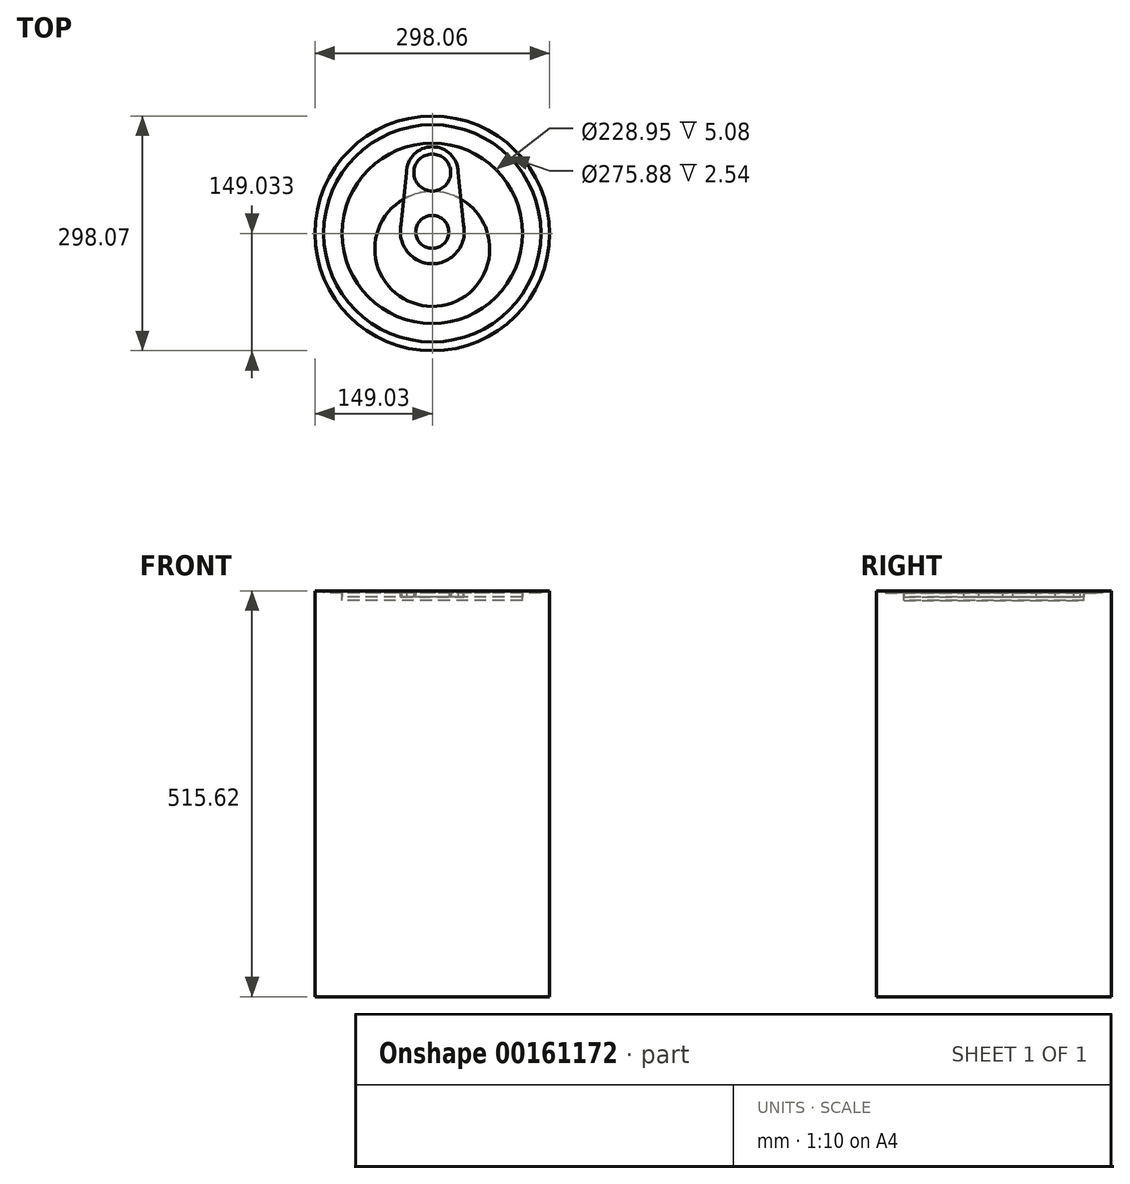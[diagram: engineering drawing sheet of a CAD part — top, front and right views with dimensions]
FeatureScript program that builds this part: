
annotation { "Feature Type Name" : "Feature", "Feature Type Description" : "" }
export const myFeature = defineFeature(function(context is Context, id is Id, definition is map)
    precondition{}
    {
        {
            var Q0;
            Q0=qCreatedBy(makeId("Top.planeOp"),FACE);
            var sketch = newSketch(context, id + "F0", { "sketchPlane" : qUnion([Q0])});
            skCircle(sketch, "E0", {"center": v(0, 0) * mm, "radius": 23.84 * mm});
            skCircle(sketch, "E1", {"center": v(0, 0) * mm, "radius": 32.37 * mm});
            skCircle(sketch, "E2", {"center": v(0, -75.39) * mm, "radius": 21.38 * mm});
            skCircle(sketch, "E3", {"center": v(0, -75.39) * mm, "radius": 40.12 * mm});
            skLineSegment(sketch, "E4", {"start": v(40.12, -76.22) * mm, "end": v(32.53, 0) * mm});
            skLineSegment(sketch, "E5", {"start": v(-32.37, 0) * mm, "end": v(-40.12, -76.25) * mm});
            skLineSegment(sketch, "E6", {"start": v(40.12, -76.22) * mm, "end": v(-40.12, -76.25) * mm});
            skLineSegment(sketch, "E7", {"start": v(32.53, 0) * mm, "end": v(-32.37, 0) * mm});
            skSolve(sketch);
        }
        {
            var Q0;
            Q0 = qSketchRegion(id + "F0", true);
            extrude(context, id + "F1", {"entities" : qUnion([Q0]), "depth" : 7.62 * mm, "hasDraft" : true, "draftAngle" : 3 * degree});
        }
        {
            var Q0;
            Q0=qCreatedBy(makeId("Top.planeOp"),FACE);
            var sketch = newSketch(context, id + "F2", { "sketchPlane" : qUnion([Q0])});
            skCircle(sketch, "E8", {"center": v(0, -77.29) * mm, "radius": 149.03 * mm});
            skSolve(sketch);
        }
        {
            var Q0;
            Q0 = qSketchRegion(id + "F2", true);
            extrude(context, id + "F3", {"entities" : qUnion([Q0]), "oppositeDirection" : true, "depth" : 508 * mm});
        }
        {
            var Q0;
            Q0=makeQuery(id+"F3.opExtrude","CAP_FACE",FACE,{"disambiguationData":[OSD([sQuery(id+"F2.wireOp",EDGE,"E8")])],"isStart":true});
            var sketch = newSketch(context, id + "F4", { "sketchPlane" : qUnion([Q0])});
            skCircle(sketch, "E9", {"center": v(0, -77.29) * mm, "radius": 137.94 * mm});
            skCircle(sketch, "E10", {"center": v(0, -77.29) * mm, "radius": 114.47 * mm});
            skSolve(sketch);
        }
        {
            var Q0;
            Q0=makeQuery(id+"F4.imprint","IMPRINT",FACE,{"disambiguationData":[TD([[makeQuery(id+"F4.imprint","IMPRINT",EDGE,{"derivedFrom":sQuery(id+"F4.wireOp",EDGE,"E9")}),1.0]])]});
            extrude(context, id + "F5", {"entities" : qUnion([Q0]), "operationType" : NewBodyOperationType.ADD, "depth" : 5.08 * mm});
        }
        {
            var Q0;
            {var subQ0=sQuery(id+"F2.wireOp",EDGE,"E8");Q0=makeQuery(id+"F5.boolean.opBoolean","SPLIT",FACE,{"disambiguationData":[TD([makeQuery(id+"F3.opExtrude","SWEPT_FACE",FACE,{"disambiguationData":[OSD([subQ0])]})])],"derivedFrom":makeQuery(id+"F3.opExtrude","CAP_FACE",FACE,{"disambiguationData":[OSD([subQ0])],"isStart":true})});}
            extrude(context, id + "F6", {"entities" : qUnion([Q0]), "operationType" : NewBodyOperationType.ADD, "depth" : 7.62 * mm});
        }
        {
            var Q0;
            Q0=makeQuery(id+"F5.opExtrude","CAP_FACE",FACE,{"disambiguationData":[OSD([sQuery(id+"F4.wireOp",EDGE,"E9"),sQuery(id+"F4.wireOp",EDGE,"E10")])],"isStart":false});
            var sketch = newSketch(context, id + "F7", { "sketchPlane" : qUnion([Q0])});
            skSolve(sketch);
        }
        {
            var Q0;
            Q0=makeQuery(id+"F7.imprint","IMPRINT",FACE,{"disambiguationData":[TD([[makeQuery(id+"F7.imprint","IMPRINT",EDGE,{"derivedFrom":makeQuery(id+"F5.opExtrude","CAP_EDGE",EDGE,{"disambiguationData":[OSD([sQuery(id+"F4.wireOp",EDGE,"E10")])],"isStart":false})}),1.0]])]});
            var sketch = newSketch(context, id + "F8", { "sketchPlane" : qUnion([Q0])});
            skCircle(sketch, "E11", {"center": v(0, -97.03) * mm, "radius": 72.96 * mm});
            skSolve(sketch);
        }
        {
            var Q0;
            Q0=makeQuery(id+"F7.imprint","IMPRINT",FACE,{"disambiguationData":[TD([[makeQuery(id+"F7.imprint","IMPRINT",EDGE,{"derivedFrom":makeQuery(id+"F5.opExtrude","CAP_EDGE",EDGE,{"disambiguationData":[OSD([sQuery(id+"F4.wireOp",EDGE,"E10")])],"isStart":false})}),1.0]])]});
            extrude(context, id + "F9", {"entities" : qUnion([Q0]), "oppositeDirection" : true, "depth" : 9.52 * mm});
        }
        {
            var Q0;
            Q0=makeQuery(id+"F8.imprint","IMPRINT",FACE,{"disambiguationData":[TD([[makeQuery(id+"F8.imprint","IMPRINT",EDGE,{"derivedFrom":sQuery(id+"F8.wireOp",EDGE,"E11")}),1.0]])]});
            extrude(context, id + "F10", {"entities" : qUnion([Q0]), "depth" : 0.25 * mm});
        }
    });
